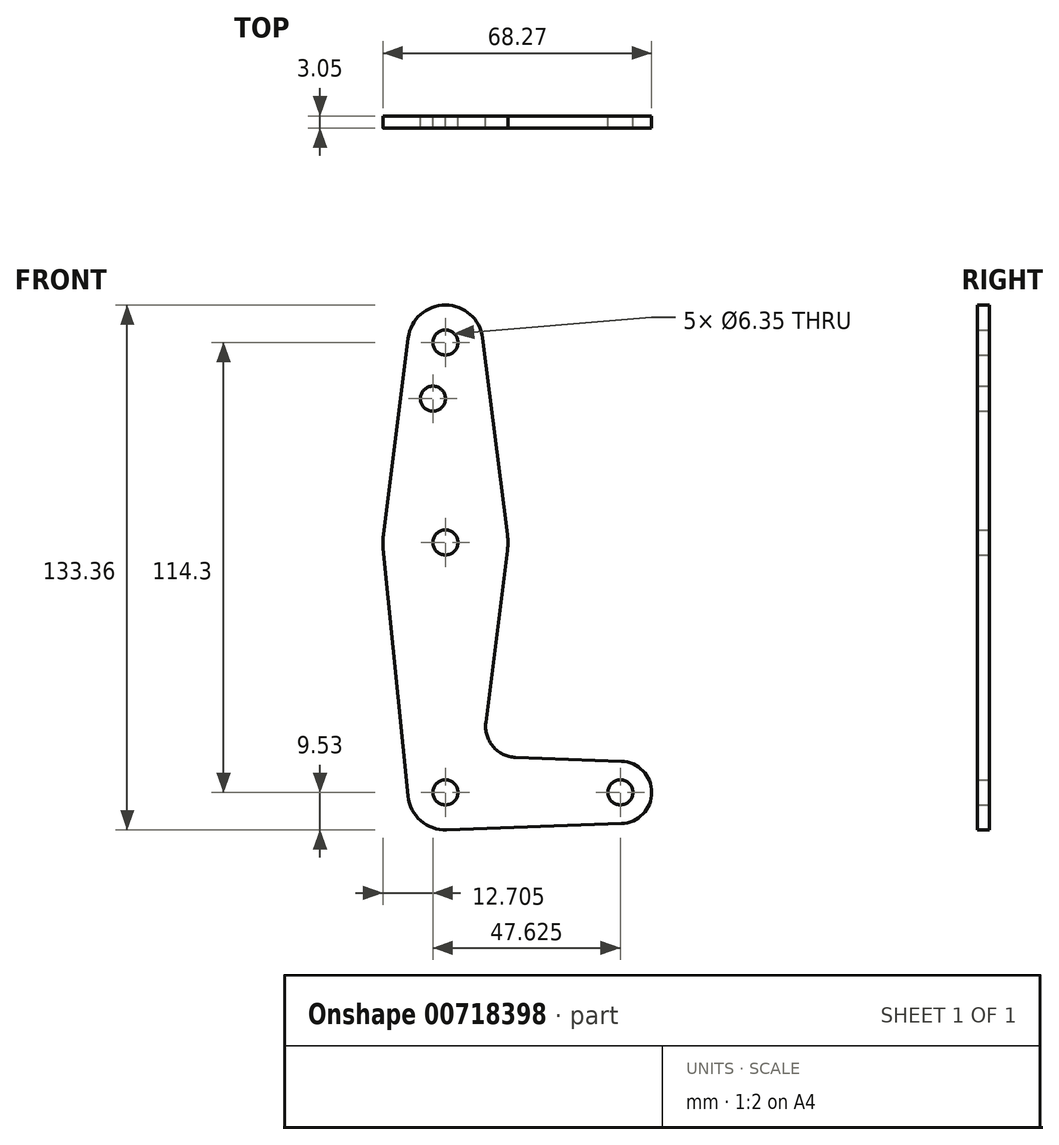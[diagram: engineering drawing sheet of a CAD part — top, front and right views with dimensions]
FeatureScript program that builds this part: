
annotation { "Feature Type Name" : "Feature", "Feature Type Description" : "" }
export const myFeature = defineFeature(function(context is Context, id is Id, definition is map)
    precondition{}
    {
        {
            var Q0;
            Q0=qCreatedBy(makeId("Front.planeOp"),FACE);
            var sketch = newSketch(context, id + "F0", { "sketchPlane" : qUnion([Q0])});
            skArc(sketch, "E0", {"start": v(-9.48, -0.95) * mm, "mid": v(-6.26, -7.18) * mm, "end": v(0.34, -9.52) * mm});
            skLineSegment(sketch, "E1", {"start": v(0, 0) * mm, "end": v(44.45, 0) * mm, "construction": true});
            skArc(sketch, "E2", {"start": v(44.73, -7.93) * mm, "mid": v(52.39, 0) * mm, "end": v(44.73, 7.93) * mm});
            skArc(sketch, "E3", {"start": v(9.45, 115.5) * mm, "mid": v(0, 123.83) * mm, "end": v(-9.45, 115.5) * mm});
            skArc(sketch, "E4", {"start": v(15.75, 61.52) * mm, "mid": v(15.88, 63.5) * mm, "end": v(15.75, 65.48) * mm});
            skLineSegment(sketch, "E5", {"start": v(17.85, 8.9) * mm, "end": v(44.73, 7.93) * mm});
            skLineSegment(sketch, "E6", {"start": v(44.73, -7.93) * mm, "end": v(0, -9.53) * mm});
            skLineSegment(sketch, "E7", {"start": v(-15.75, 65.48) * mm, "end": v(-9.45, 115.5) * mm});
            skLineSegment(sketch, "E8", {"start": v(9.45, 115.5) * mm, "end": v(15.75, 65.48) * mm});
            skLineSegment(sketch, "E9", {"start": v(15.75, 61.52) * mm, "end": v(10.25, 17.83) * mm});
            skArc(sketch, "E10.filletArc", {"start": v(10.25, 17.83) * mm, "mid": v(12.08, 11.69) * mm, "end": v(17.85, 8.9) * mm});
            skCircle(sketch, "E11", {"center": v(0, 114.3) * mm, "radius": 3.18 * mm});
            skCircle(sketch, "E12", {"center": v(0, 63.5) * mm, "radius": 3.18 * mm});
            skCircle(sketch, "E13", {"center": v(0, 0) * mm, "radius": 3.18 * mm});
            skCircle(sketch, "E14", {"center": v(44.45, 0) * mm, "radius": 3.18 * mm});
            skCircle(sketch, "E15", {"center": v(-3.18, 100.03) * mm, "radius": 3.18 * mm});
            skLineSegment(sketch, "E16", {"start": v(-15.8, 61.91) * mm, "end": v(-9.48, -0.95) * mm});
            skLineSegment(sketch, "E17", {"start": v(0, 63.5) * mm, "end": v(0, 138.31) * mm, "construction": true});
            skLineSegment(sketch, "E18", {"start": v(0, 63.5) * mm, "end": v(0, -38.87) * mm, "construction": true});
            skArc(sketch, "E19.trimOffspring", {"start": v(-15.75, 65.48) * mm, "mid": v(-15.87, 63.7) * mm, "end": v(-15.8, 61.91) * mm});
            skSolve(sketch);
        }
        {
            var Q0;
            Q0 = qSketchRegion(id + "F0", true);
            extrude(context, id + "F1", {"entities" : qUnion([Q0]), "depth" : 3.05 * mm, "offsetDistance" : 25.4 * mm});
        }
    });
